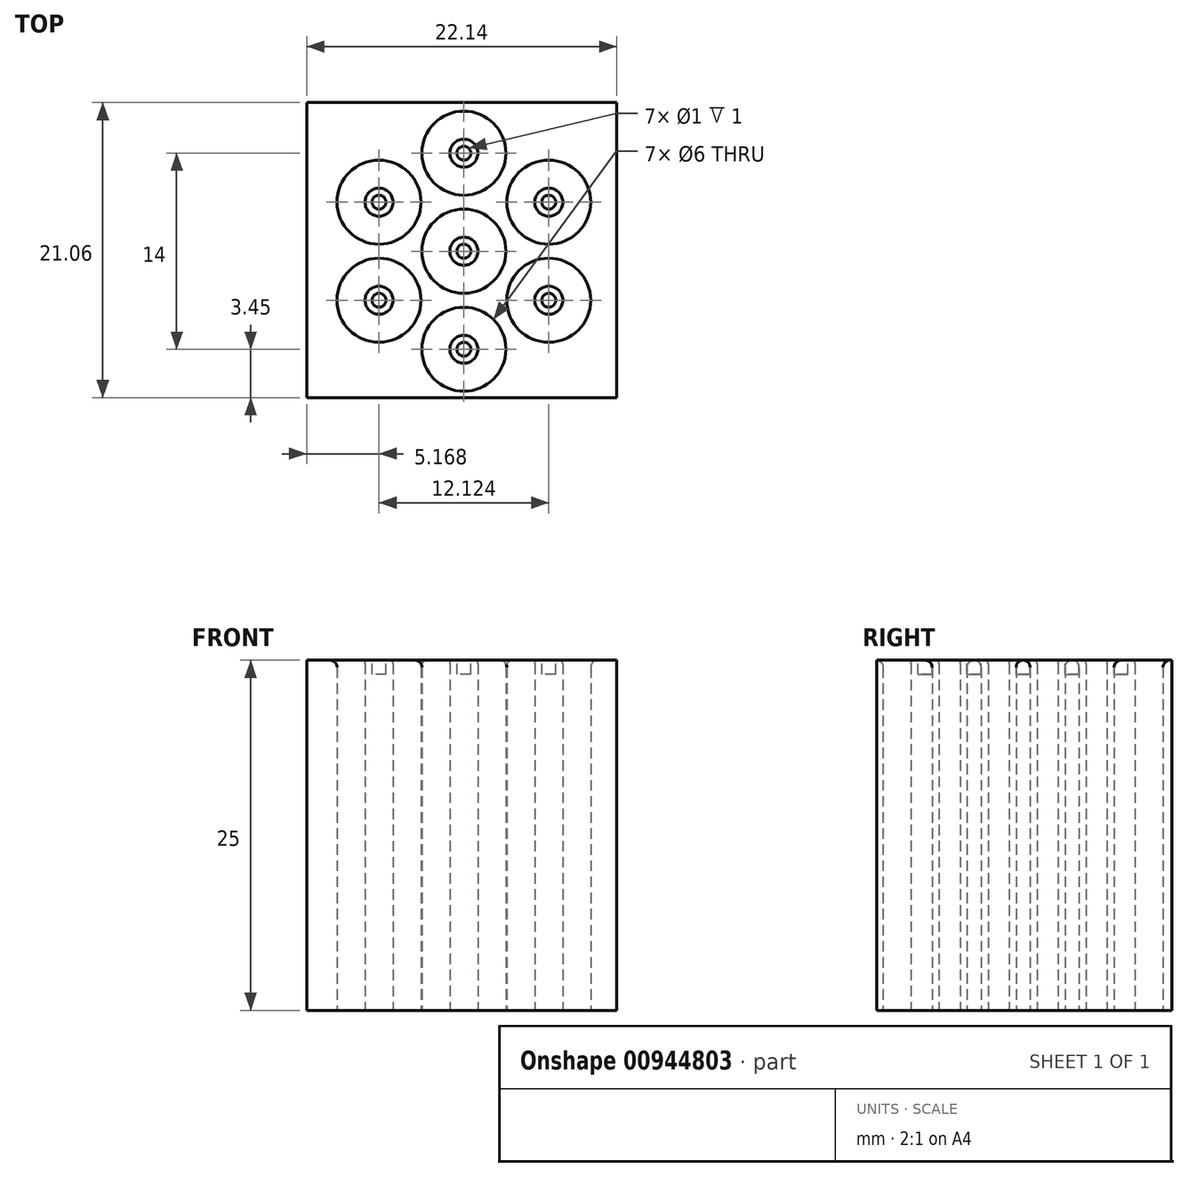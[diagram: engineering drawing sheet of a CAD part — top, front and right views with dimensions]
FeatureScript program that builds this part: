
annotation { "Feature Type Name" : "Feature", "Feature Type Description" : "" }
export const myFeature = defineFeature(function(context is Context, id is Id, definition is map)
    precondition{}
    {
        {
            var Q0;
            Q0=qCreatedBy(makeId("Top.planeOp"),FACE);
            var sketch = newSketch(context, id + "F0", { "sketchPlane" : qUnion([Q0])});
            skCircle(sketch, "E0", {"center": v(0, 0) * mm, "radius": 3 * mm});
            skCircle(sketch, "E1", {"center": v(0, 7) * mm, "radius": 3 * mm});
            skCircle(sketch, "E2.1.0", {"center": v(-6.06, 3.5) * mm, "radius": 3 * mm});
            skCircle(sketch, "E2.2.0", {"center": v(-6.06, -3.5) * mm, "radius": 3 * mm});
            skCircle(sketch, "E2.3.0", {"center": v(0, -7) * mm, "radius": 3 * mm});
            skCircle(sketch, "E2.4.0", {"center": v(6.06, -3.5) * mm, "radius": 3 * mm});
            skCircle(sketch, "E2.5.0", {"center": v(6.06, 3.5) * mm, "radius": 3 * mm});
            skCircle(sketch, "E3", {"center": v(0, 0) * mm, "radius": 1 * mm});
            skCircle(sketch, "E4", {"center": v(0, 7) * mm, "radius": 1 * mm});
            skCircle(sketch, "E5.1.0", {"center": v(-6.06, 3.5) * mm, "radius": 1 * mm});
            skCircle(sketch, "E5.2.0", {"center": v(-6.06, -3.5) * mm, "radius": 1 * mm});
            skCircle(sketch, "E5.3.0", {"center": v(0, -7) * mm, "radius": 1 * mm});
            skCircle(sketch, "E5.4.0", {"center": v(6.06, -3.5) * mm, "radius": 1 * mm});
            skCircle(sketch, "E5.5.0", {"center": v(6.06, 3.5) * mm, "radius": 1 * mm});
            skLineSegment(sketch, "E6.bottom", {"start": v(-11.23, 10.61) * mm, "end": v(10.9, 10.61) * mm});
            skLineSegment(sketch, "E6.top", {"start": v(-11.23, -10.45) * mm, "end": v(10.9, -10.45) * mm});
            skLineSegment(sketch, "E6.left", {"start": v(-11.23, 10.61) * mm, "end": v(-11.23, -10.45) * mm});
            skLineSegment(sketch, "E6.right", {"start": v(10.9, 10.61) * mm, "end": v(10.9, -10.45) * mm});
            skSolve(sketch);
        }
        {
            var Q0;
            Q0=makeQuery(id+"F0.imprint","IMPRINT",FACE,{"disambiguationData":[TD([[makeQuery(id+"F0.imprint","IMPRINT",EDGE,{"derivedFrom":sQuery(id+"F0.wireOp",EDGE,"E5.2.0")}),1.0]])]});
            var Q1;
            Q1=makeQuery(id+"F0.imprint","IMPRINT",FACE,{"disambiguationData":[TD([[makeQuery(id+"F0.imprint","IMPRINT",EDGE,{"derivedFrom":sQuery(id+"F0.wireOp",EDGE,"E3")}),1.0]])]});
            var Q2;
            Q2=makeQuery(id+"F0.imprint","IMPRINT",FACE,{"disambiguationData":[TD([[makeQuery(id+"F0.imprint","IMPRINT",EDGE,{"derivedFrom":sQuery(id+"F0.wireOp",EDGE,"E5.3.0")}),1.0]])]});
            var Q3;
            Q3=makeQuery(id+"F0.imprint","IMPRINT",FACE,{"disambiguationData":[TD([[makeQuery(id+"F0.imprint","IMPRINT",EDGE,{"derivedFrom":sQuery(id+"F0.wireOp",EDGE,"E5.4.0")}),1.0]])]});
            var Q4;
            Q4=makeQuery(id+"F0.imprint","IMPRINT",FACE,{"disambiguationData":[TD([[makeQuery(id+"F0.imprint","IMPRINT",EDGE,{"derivedFrom":sQuery(id+"F0.wireOp",EDGE,"E5.5.0")}),1.0]])]});
            var Q5;
            Q5=makeQuery(id+"F0.imprint","IMPRINT",FACE,{"disambiguationData":[TD([[makeQuery(id+"F0.imprint","IMPRINT",EDGE,{"derivedFrom":sQuery(id+"F0.wireOp",EDGE,"E5.1.0")}),1.0]])]});
            var Q6;
            Q6=makeQuery(id+"F0.imprint","IMPRINT",FACE,{"disambiguationData":[TD([[makeQuery(id+"F0.imprint","IMPRINT",EDGE,{"derivedFrom":sQuery(id+"F0.wireOp",EDGE,"E4")}),1.0]])]});
            var Q7;
            Q7=makeQuery(id+"F0.imprint","IMPRINT",FACE,{"disambiguationData":[TD([[makeQuery(id+"F0.imprint","IMPRINT",EDGE,{"derivedFrom":sQuery(id+"F0.wireOp",EDGE,"E0")}),-1.0]])]});
            extrude(context, id + "F1", {"entities" : qUnion([Q0, Q1, Q2, Q3, Q4, Q5, Q6, Q7]), "depth" : 25 * mm, "offsetDistance" : 25 * mm});
        }
        {
            var Q0;
            Q0=makeQuery(id+"F1.opExtrude","CAP_EDGE",EDGE,{"disambiguationData":[OSD([sQuery(id+"F0.wireOp",EDGE,"E5.5.0")])],"isStart":false});
            var Q1;
            Q1=makeQuery(id+"F1.opExtrude","CAP_EDGE",EDGE,{"disambiguationData":[OSD([sQuery(id+"F0.wireOp",EDGE,"E5.4.0")])],"isStart":false});
            var Q2;
            Q2=makeQuery(id+"F1.opExtrude","CAP_EDGE",EDGE,{"disambiguationData":[OSD([sQuery(id+"F0.wireOp",EDGE,"E5.3.0")])],"isStart":false});
            var Q3;
            Q3=makeQuery(id+"F1.opExtrude","CAP_EDGE",EDGE,{"disambiguationData":[OSD([sQuery(id+"F0.wireOp",EDGE,"E3")])],"isStart":false});
            var Q4;
            Q4=makeQuery(id+"F1.opExtrude","CAP_EDGE",EDGE,{"disambiguationData":[OSD([sQuery(id+"F0.wireOp",EDGE,"E5.2.0")])],"isStart":false});
            var Q5;
            Q5=makeQuery(id+"F1.opExtrude","CAP_EDGE",EDGE,{"disambiguationData":[OSD([sQuery(id+"F0.wireOp",EDGE,"E5.1.0")])],"isStart":false});
            var Q6;
            Q6=makeQuery(id+"F1.opExtrude","CAP_EDGE",EDGE,{"disambiguationData":[OSD([sQuery(id+"F0.wireOp",EDGE,"E4")])],"isStart":false});
            fillet(context, id + "F2", {"entities" : qUnion([Q0, Q1, Q2, Q3, Q4, Q5, Q6]), "radius" : 0.25 * mm, "tangentPropagation" : true, "allowEdgeOverflow" : false});
        }
        {
            var Q0;
            Q0=makeQuery(id+"F1.opExtrude","CAP_FACE",FACE,{"disambiguationData":[OSD([sQuery(id+"F0.wireOp",EDGE,"E3")])],"isStart":false});
            var sketch = newSketch(context, id + "F3", { "sketchPlane" : qUnion([Q0])});
            skCircle(sketch, "E7", {"center": v(0, 0) * mm, "radius": 0.5 * mm});
            skCircle(sketch, "E8", {"center": v(0, -7) * mm, "radius": 0.5 * mm});
            skCircle(sketch, "E9.1.0", {"center": v(6.06, -3.5) * mm, "radius": 0.5 * mm});
            skCircle(sketch, "E9.2.0", {"center": v(6.06, 3.5) * mm, "radius": 0.5 * mm});
            skCircle(sketch, "E9.3.0", {"center": v(0, 7) * mm, "radius": 0.5 * mm});
            skCircle(sketch, "E9.4.0", {"center": v(-6.06, 3.5) * mm, "radius": 0.5 * mm});
            skCircle(sketch, "E9.5.0", {"center": v(-6.06, -3.5) * mm, "radius": 0.5 * mm});
            skSolve(sketch);
        }
        {
            var Q0;
            Q0 = qSketchRegion(id + "F3", true);
            extrude(context, id + "F4", {"entities" : qUnion([Q0]), "operationType" : NewBodyOperationType.REMOVE, "oppositeDirection" : true, "depth" : 1 * mm, "offsetDistance" : 25 * mm});
        }
        {
            var Q0;
            Q0=makeQuery(id+"F1.opExtrude","CAP_EDGE",EDGE,{"disambiguationData":[OSD([sQuery(id+"F0.wireOp",EDGE,"E2.5.0")])],"isStart":false});
            var Q1;
            Q1=makeQuery(id+"F1.opExtrude","CAP_EDGE",EDGE,{"disambiguationData":[OSD([sQuery(id+"F0.wireOp",EDGE,"E2.4.0")])],"isStart":false});
            var Q2;
            Q2=makeQuery(id+"F1.opExtrude","CAP_EDGE",EDGE,{"disambiguationData":[OSD([sQuery(id+"F0.wireOp",EDGE,"E0")])],"isStart":false});
            var Q3;
            Q3=makeQuery(id+"F1.opExtrude","CAP_EDGE",EDGE,{"disambiguationData":[OSD([sQuery(id+"F0.wireOp",EDGE,"E2.3.0")])],"isStart":false});
            var Q4;
            Q4=makeQuery(id+"F1.opExtrude","CAP_EDGE",EDGE,{"disambiguationData":[OSD([sQuery(id+"F0.wireOp",EDGE,"E2.2.0")])],"isStart":false});
            var Q5;
            Q5=makeQuery(id+"F1.opExtrude","CAP_EDGE",EDGE,{"disambiguationData":[OSD([sQuery(id+"F0.wireOp",EDGE,"E2.1.0")])],"isStart":false});
            var Q6;
            Q6=makeQuery(id+"F1.opExtrude","CAP_EDGE",EDGE,{"disambiguationData":[OSD([sQuery(id+"F0.wireOp",EDGE,"E1")])],"isStart":false});
            fillet(context, id + "F5", {"entities" : qUnion([Q0, Q1, Q2, Q3, Q4, Q5, Q6]), "radius" : 0.5 * mm, "tangentPropagation" : true, "allowEdgeOverflow" : false});
        }
    });
